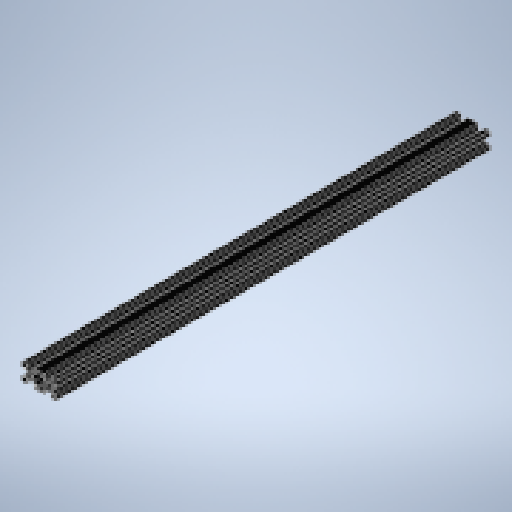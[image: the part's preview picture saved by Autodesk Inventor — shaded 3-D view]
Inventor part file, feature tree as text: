
AUTODESK INVENTOR PART (.ipt)
format: ipt  version: 2025.1 (Build 291241020, 241B)  size: 546,304 bytes
history: native  units: in
note: dims shown in document units (in); Inventor stores cm internally (conversion verified against a paired STEP export)
features: projected_geometry x102, plane x1, extrude x1, sketch x1
ambient origin geometry x8: Origin, YZ Plane, XZ Plane, XY Plane, X Axis, Y Axis, Z Axis, Center Point
bodies: Solid1 (feature_tree)
feature tree (105):
  plane  "Work Plane2"
  extrude  "Extrusion1"  [1 undecoded]
  sketch  "Sketch1"  dims[d0=19.685in d1=0.0in]
  projected_geometry  "Projected Loop1"
  projected_geometry  "Projected Loop2"
  projected_geometry  "Projected Loop3"
  projected_geometry  "Projected Loop4"
  projected_geometry  "Projected Loop5"
  projected_geometry  "Projected Loop6"
  projected_geometry  "Projected Loop7"
  projected_geometry  "Projected Loop8"
  projected_geometry  "Projected Loop9"
  projected_geometry  "Projected Loop10"
  projected_geometry  "Projected Loop11"
  projected_geometry  "Projected Loop12"
  projected_geometry  "Projected Loop13"
  projected_geometry  "Projected Loop14"
  projected_geometry  "Projected Loop15"
  projected_geometry  "Projected Loop16"
  projected_geometry  "Projected Loop17"
  projected_geometry  "Projected Loop18"
  projected_geometry  "Projected Loop19"
  projected_geometry  "Projected Loop20"
  projected_geometry  "Projected Loop21"
  projected_geometry  "Projected Loop22"
  projected_geometry  "Projected Loop23"
  projected_geometry  "Projected Loop24"
  projected_geometry  "Projected Loop25"
  projected_geometry  "Projected Loop26"
  projected_geometry  "Projected Loop27"
  projected_geometry  "Projected Loop28"
  projected_geometry  "Projected Loop29"
  projected_geometry  "Projected Loop30"
  projected_geometry  "Projected Loop31"
  projected_geometry  "Projected Loop32"
  projected_geometry  "Projected Loop33"
  projected_geometry  "Projected Loop34"
  projected_geometry  "Projected Loop35"
  projected_geometry  "Projected Loop36"
  projected_geometry  "Projected Loop37"
  projected_geometry  "Projected Loop38"
  projected_geometry  "Projected Loop39"
  projected_geometry  "Projected Loop40"
  projected_geometry  "Projected Loop41"
  projected_geometry  "Projected Loop42"
  projected_geometry  "Projected Loop43"
  projected_geometry  "Projected Loop44"
  projected_geometry  "Projected Loop45"
  projected_geometry  "Projected Loop46"
  projected_geometry  "Projected Loop47"
  projected_geometry  "Projected Loop48"
  projected_geometry  "Projected Loop49"
  projected_geometry  "Projected Loop50"
  projected_geometry  "Projected Loop51"
  projected_geometry  "Projected Loop52"
  projected_geometry  "Projected Loop53"
  projected_geometry  "Projected Loop54"
  projected_geometry  "Projected Loop55"
  projected_geometry  "Projected Loop56"
  projected_geometry  "Projected Loop57"
  projected_geometry  "Projected Loop58"
  projected_geometry  "Projected Loop59"
  projected_geometry  "Projected Loop60"
  projected_geometry  "Projected Loop61"
  projected_geometry  "Projected Loop62"
  projected_geometry  "Projected Loop63"
  projected_geometry  "Projected Loop64"
  projected_geometry  "Projected Loop65"
  projected_geometry  "Projected Loop66"
  projected_geometry  "Projected Loop67"
  projected_geometry  "Projected Loop68"
  projected_geometry  "Projected Loop69"
  projected_geometry  "Projected Loop70"
  projected_geometry  "Projected Loop71"
  projected_geometry  "Projected Loop72"
  projected_geometry  "Projected Loop73"
  projected_geometry  "Projected Loop74"
  projected_geometry  "Projected Loop75"
  projected_geometry  "Projected Loop76"
  projected_geometry  "Projected Loop77"
  projected_geometry  "Projected Loop78"
  projected_geometry  "Projected Loop79"
  projected_geometry  "Projected Loop80"
  projected_geometry  "Projected Loop81"
  projected_geometry  "Projected Loop82"
  projected_geometry  "Projected Loop83"
  projected_geometry  "Projected Loop84"
  projected_geometry  "Projected Loop85"
  projected_geometry  "Projected Loop86"
  projected_geometry  "Projected Loop87"
  projected_geometry  "Projected Loop88"
  projected_geometry  "Projected Loop89"
  projected_geometry  "Projected Loop90"
  projected_geometry  "Projected Loop91"
  projected_geometry  "Projected Loop92"
  projected_geometry  "Projected Loop93"
  projected_geometry  "Projected Loop94"
  projected_geometry  "Projected Loop95"
  projected_geometry  "Projected Loop96"
  projected_geometry  "Projected Loop97"
  projected_geometry  "Projected Loop98"
  projected_geometry  "Projected Loop99"
  projected_geometry  "Projected Loop100"
  projected_geometry  "Projected Loop101"
  projected_geometry  "Projected Loop102"
note: 1 required parameter value undecoded (feature->parameter linkage not recoverable at this tier; creation-order binding heuristic only, values carry confidence <= 0.55)
